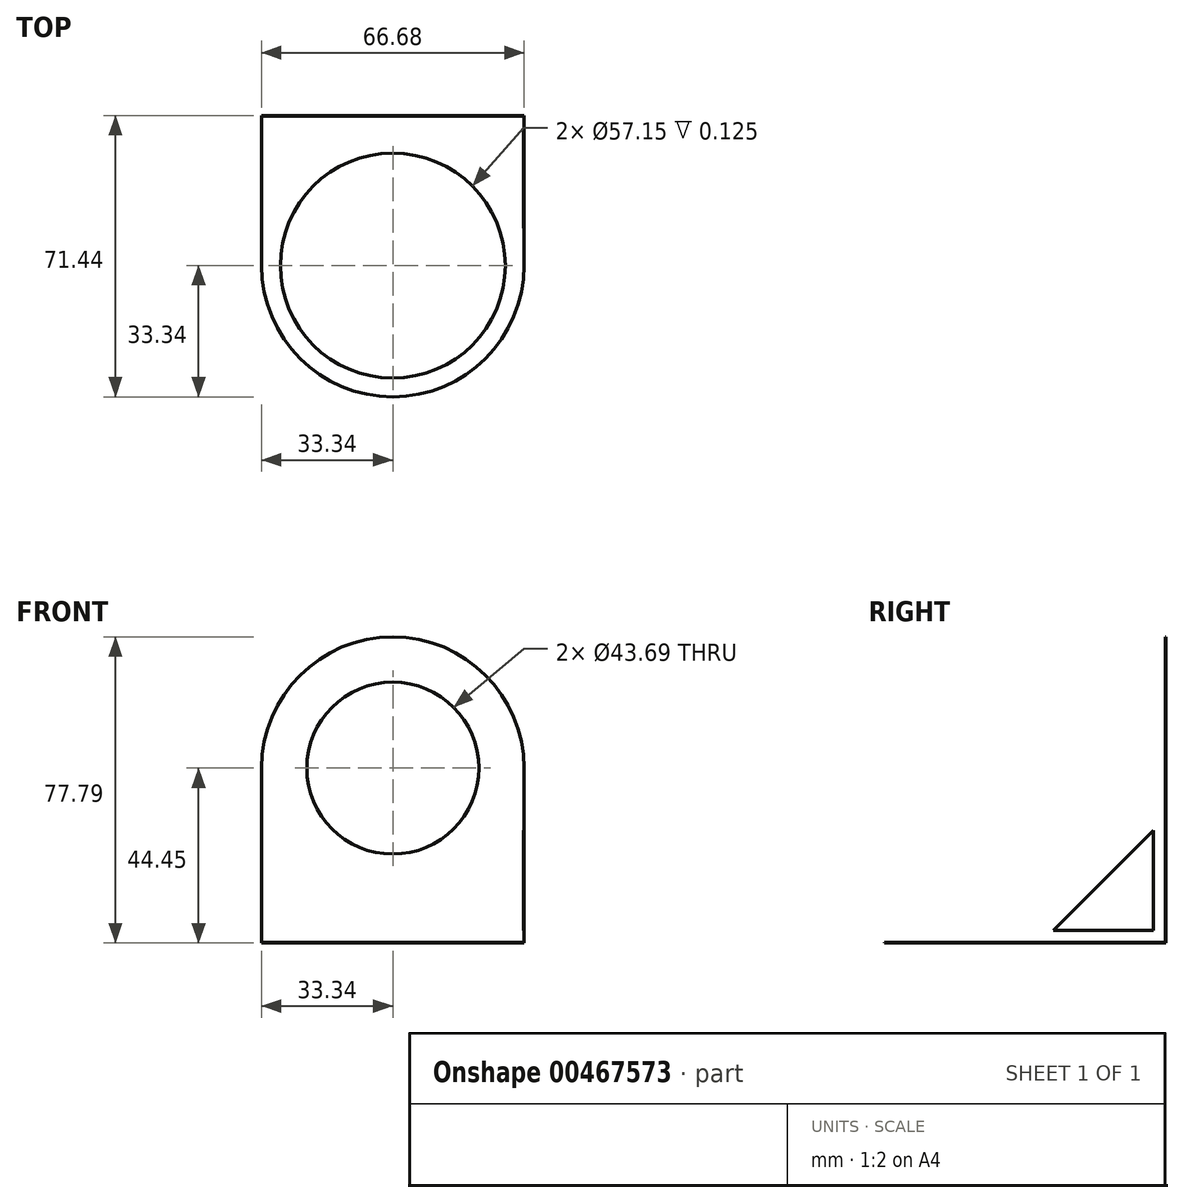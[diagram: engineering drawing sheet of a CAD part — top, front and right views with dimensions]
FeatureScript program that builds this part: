
annotation { "Feature Type Name" : "Feature", "Feature Type Description" : "" }
export const myFeature = defineFeature(function(context is Context, id is Id, definition is map)
    precondition{}
    {
        {
            assignVariable(context, id + "F0", {"name" : "thk", "anyValue" : .125});
        }
        {
            var Q0;
            Q0=qCreatedBy(makeId("Front.planeOp"),FACE);
            var sketch = newSketch(context, id + "F1", { "sketchPlane" : qUnion([Q0])});
            skCircle(sketch, "E0", {"center": v(0, 44.45) * mm, "radius": 21.84 * mm});
            skArc(sketch, "E1.0", {"start": v(33.34, 44.45) * mm, "mid": v(0, 77.79) * mm, "end": v(-33.34, 44.45) * mm});
            skLineSegment(sketch, "E2", {"start": v(-33.34, 44.45) * mm, "end": v(-33.34, 0) * mm});
            skLineSegment(sketch, "E3", {"start": v(-33.34, 0) * mm, "end": v(33.34, 0) * mm});
            skLineSegment(sketch, "E4", {"start": v(33.34, 0) * mm, "end": v(33.34, 44.45) * mm});
            skSolve(sketch);
        }
        {
            var Q0;
            Q0=makeQuery(id+"F1.imprint","IMPRINT",FACE,{"disambiguationData":[TD([[makeQuery(id+"F1.imprint","IMPRINT",EDGE,{"derivedFrom":sQuery(id+"F1.wireOp",EDGE,"E0")}),-1.0]])]});
            extrude(context, id + "F2", {"entities" : qUnion([Q0]), "depth" : (getVariable(context, 'thk')) * mm});
        }
        {
            var Q0;
            Q0=makeQuery(id+"F2.opExtrude","SWEPT_FACE",FACE,{"disambiguationData":[OSD([sQuery(id+"F1.wireOp",EDGE,"E3")])]});
            var sketch = newSketch(context, id + "F3", { "sketchPlane" : qUnion([Q0])});
            skLineSegment(sketch, "E5.bottom", {"start": v(-33.34, 0) * mm, "end": v(33.34, 0) * mm});
            skLineSegment(sketch, "E5.left", {"start": v(-33.34, 0) * mm, "end": v(-33.34, 38.1) * mm});
            skLineSegment(sketch, "E5.right", {"start": v(33.34, 0) * mm, "end": v(33.34, 38.1) * mm});
            skArc(sketch, "E6", {"start": v(33.34, 38.1) * mm, "mid": v(0, 71.44) * mm, "end": v(-33.34, 38.1) * mm});
            skCircle(sketch, "E7", {"center": v(0, 38.1) * mm, "radius": 28.58 * mm});
            skSolve(sketch);
        }
        {
            var Q0;
            {var subQ0=sQuery(id+"F3.wireOp",EDGE,"E6");Q0=makeQuery(id+"F3.imprint","IMPRINT",FACE,{"disambiguationData":[TD([[makeQuery(id+"F3.imprint","IMPRINT",EDGE,{"derivedFrom":subQ0}),1.0]])]});}
            extrude(context, id + "F4", {"entities" : qUnion([Q0]), "operationType" : NewBodyOperationType.ADD, "oppositeDirection" : true, "depth" : (getVariable(context, 'thk')) * mm});
        }
        {
            var Q0;
            Q0=makeQuery(id+"F4.boolean.opBoolean","MERGE",FACE,{"derivedFrom":[makeQuery(id+"F2.opExtrude","SWEPT_FACE",FACE,{"disambiguationData":[OSD([sQuery(id+"F1.wireOp",EDGE,"E4")])]}),makeQuery(id+"F4.opExtrude","SWEPT_FACE",FACE,{"disambiguationData":[OSD([sQuery(id+"F3.wireOp",EDGE,"E5.right")])]})]});
            var sketch = newSketch(context, id + "F5", { "sketchPlane" : qUnion([Q0])});
            skLineSegment(sketch, "E8", {"start": v(-3.18, 28.57) * mm, "end": v(-28.58, 3.17) * mm});
            skLineSegment(sketch, "E9", {"start": v(-28.58, 3.17) * mm, "end": v(-3.18, 3.17) * mm});
            skLineSegment(sketch, "E10", {"start": v(-3.18, 3.17) * mm, "end": v(-3.18, 28.57) * mm});
            skSolve(sketch);
        }
        {
            var Q0;
            Q0=makeQuery(id+"F5.imprint","IMPRINT",FACE,{"disambiguationData":[TD([[makeQuery(id+"F5.imprint","IMPRINT",EDGE,{"derivedFrom":sQuery(id+"F5.wireOp",EDGE,"E8")}),1.0]])]});
            extrude(context, id + "F6", {"entities" : qUnion([Q0]), "operationType" : NewBodyOperationType.ADD, "oppositeDirection" : true, "depth" : (getVariable(context, 'thk')) * mm});
        }
        {
            var Q0;
            Q0=makeQuery(id+"F2.opExtrude","SWEPT_BODY",BODY,{"disambiguationData":[OSD([sQuery(id+"F1.wireOp",EDGE,"E0"),sQuery(id+"F1.wireOp",EDGE,"E1.0"),sQuery(id+"F1.wireOp",EDGE,"E2"),sQuery(id+"F1.wireOp",EDGE,"E3"),sQuery(id+"F1.wireOp",EDGE,"E4")])]});
            var Q1;
            Q1=qCreatedBy(makeId("Right.planeOp"),FACE);
            mirror(context, id + "F7", {"operationType" : NewBodyOperationType.ADD, "entities" : qUnion([Q0]), "mirrorPlane" : qUnion([Q1])});
        }
    });
